# Revit family: FM3.402
name_source: partatom
category: Plumbing Fixtures
revit_build: Autodesk Revit Architecture 2012 (Build: 20110309_2315(x64)
units: mm (PartAtom-declared; Revit-internal decimal feet)

## types (1)
- FM3.402
    Assembly Code = D2010
    CW Connection = Yes
    CWFU = 0
    Control stop assembly = C-FMC1.3
    Cost = 0 $
    Default Elevation = 0' - 0"
    Description = Concealed type. Back entry + palm press, connector and control stop
    Elbow connector = C-FM8.45
    Flushpipe = FMT3.4CP
    HW Connection = Yes
    HWFU = 0
    Keynote = Palm press pushbutton assembly with pushrod
    Manufacturer = COBRA
    Material = DZR Brass
    Model = FM3.402
    Palm press pushbutton assembly with pushrod = C-KM9.14
    Piston assembly = C-FM8.30
    Plunger assembly = C-FM8.60
    Range = Standard Flushmaster Flushvalves
    Rod = C-FMR1.015
    Rubber pan connector = C-FMV8.3
    Top cover assembly = C-FMC1.2
    Type Comments = SANS 1240
    URL = http://www.cobra.co.za
    Vent Connection = No
    WFU = 0
    Waste Connection = No

## geometry (parser evidence)
native form markers: Blend x5
no freeform markers — native parametric forms only
